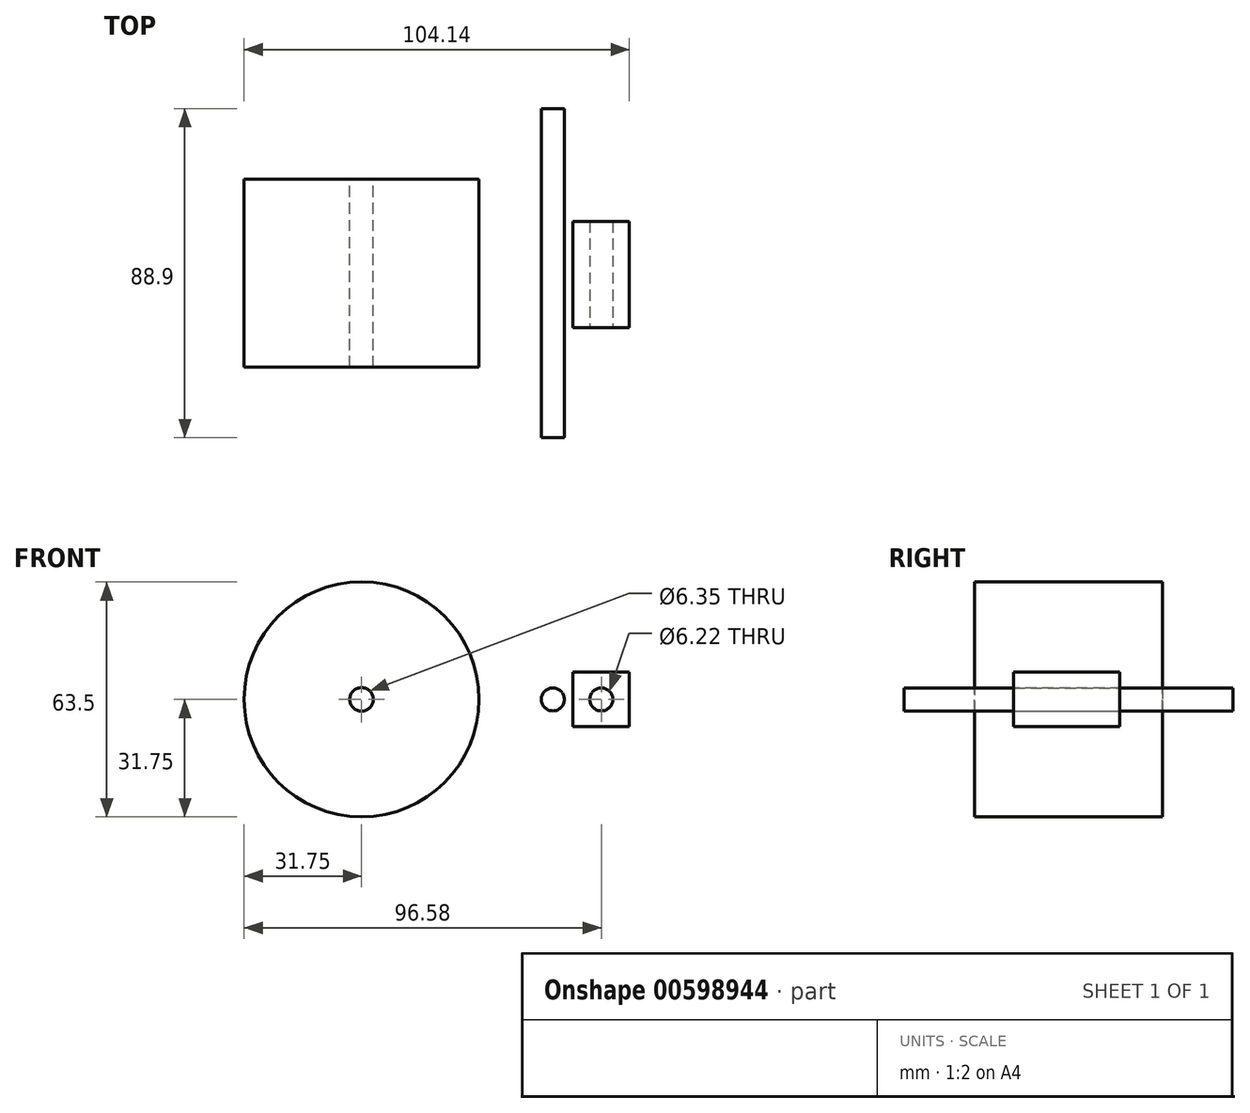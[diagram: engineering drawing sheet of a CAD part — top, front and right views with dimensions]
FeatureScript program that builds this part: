
annotation { "Feature Type Name" : "Feature", "Feature Type Description" : "" }
export const myFeature = defineFeature(function(context is Context, id is Id, definition is map)
    precondition{}
    {
        {
            var Q0;
            Q0=qCreatedBy(makeId("Front.planeOp"),FACE);
            var sketch = newSketch(context, id + "F0", { "sketchPlane" : qUnion([Q0])});
            skCircle(sketch, "E0", {"center": v(0, 0) * mm, "radius": 31.75 * mm});
            skCircle(sketch, "E1", {"center": v(51.7, 0) * mm, "radius": 3.11 * mm});
            skSolve(sketch);
        }
        {
            var Q0;
            Q0=makeQuery(id+"F0.imprint","IMPRINT",FACE,{"disambiguationData":[TD([[makeQuery(id+"F0.imprint","IMPRINT",EDGE,{"derivedFrom":sQuery(id+"F0.wireOp",EDGE,"E0")}),1.0]])]});
            extrude(context, id + "F1", {"entities" : qUnion([Q0]), "depth" : 50.8 * mm, "offsetDistance" : 25.4 * mm});
        }
        {
            var Q0;
            Q0=makeQuery(id+"F1.opExtrude","CAP_FACE",FACE,{"disambiguationData":[OSD([sQuery(id+"F0.wireOp",EDGE,"E0")])],"isStart":true});
            var sketch = newSketch(context, id + "F2", { "sketchPlane" : qUnion([Q0])});
            skCircle(sketch, "E2", {"center": v(0, 0) * mm, "radius": 3.18 * mm});
            skSolve(sketch);
        }
        {
            var Q0;
            Q0=makeQuery(id+"F2.imprint","IMPRINT",FACE,{"disambiguationData":[TD([[makeQuery(id+"F2.imprint","IMPRINT",EDGE,{"derivedFrom":sQuery(id+"F2.wireOp",EDGE,"E2")}),1.0]])]});
            extrude(context, id + "F3", {"entities" : qUnion([Q0]), "operationType" : NewBodyOperationType.REMOVE, "endBound" : BoundingType.THROUGH_ALL, "oppositeDirection" : true, "depth" : 25.4 * mm, "offsetDistance" : 25.4 * mm});
        }
        {
            var Q0;
            Q0=makeQuery(id+"F0.imprint","IMPRINT",FACE,{"disambiguationData":[TD([[makeQuery(id+"F0.imprint","IMPRINT",EDGE,{"derivedFrom":sQuery(id+"F0.wireOp",EDGE,"E1")}),1.0]])]});
            extrude(context, id + "F4", {"entities" : qUnion([Q0]), "depth" : 69.85 * mm, "offsetDistance" : 25.4 * mm, "hasSecondDirection" : true, "secondDirectionOppositeDirection" : true, "secondDirectionDepth" : 19.05 * mm});
        }
        {
            var Q0;
            Q0=qCreatedBy(makeId("Right.planeOp"),FACE);
            var sketch = newSketch(context, id + "F5", { "sketchPlane" : qUnion([Q0])});
            skLineSegment(sketch, "E3.bottom", {"start": v(-40.14, 7.44) * mm, "end": v(-11.44, 7.44) * mm});
            skLineSegment(sketch, "E3.top", {"start": v(-40.14, -7.37) * mm, "end": v(-11.44, -7.37) * mm});
            skLineSegment(sketch, "E3.left", {"start": v(-40.14, 7.44) * mm, "end": v(-40.14, -7.37) * mm});
            skLineSegment(sketch, "E3.right", {"start": v(-11.44, 7.44) * mm, "end": v(-11.44, -7.37) * mm});
            skSolve(sketch);
        }
        {
            var Q0;
            Q0 = qSketchRegion(id + "F5", true);
            extrude(context, id + "F6", {"entities" : qUnion([Q0]), "operationType" : NewBodyOperationType.ADD, "depth" : 72.39 * mm, "offsetDistance" : 25.4 * mm, "hasSecondDirection" : true, "secondDirectionOppositeDirection" : false, "secondDirectionDepth" : 57.15 * mm});
        }
        {
            var Q0;
            Q0=makeQuery(id+"F6.opExtrude","SWEPT_FACE",FACE,{"disambiguationData":[OSD([sQuery(id+"F5.wireOp",EDGE,"E3.left")])]});
            var sketch = newSketch(context, id + "F7", { "sketchPlane" : qUnion([Q0])});
            skCircle(sketch, "E4", {"center": v(64.83, 0) * mm, "radius": 3.11 * mm});
            skSolve(sketch);
        }
        {
            var Q0;
            Q0=makeQuery(id+"F7.imprint","IMPRINT",FACE,{"disambiguationData":[TD([[makeQuery(id+"F7.imprint","IMPRINT",EDGE,{"derivedFrom":sQuery(id+"F7.wireOp",EDGE,"E4")}),1.0]])]});
            extrude(context, id + "F8", {"entities" : qUnion([Q0]), "operationType" : NewBodyOperationType.REMOVE, "endBound" : BoundingType.THROUGH_ALL, "oppositeDirection" : true, "depth" : 25.4 * mm, "offsetDistance" : 25.4 * mm});
        }
    });
